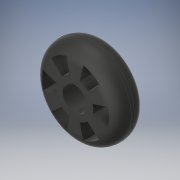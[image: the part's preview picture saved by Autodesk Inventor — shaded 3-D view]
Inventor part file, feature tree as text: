
AUTODESK INVENTOR PART (.ipt)
format: ipt  version: 2017 SP1 (Build 210196100, 196)  size: 229,888 bytes
history: native  units: in
note: dims shown in document units (in); Inventor stores cm internally (conversion verified against a paired STEP export)
features: extrude x1, fillet x1, sketch x1
ambient origin geometry x8: Origin, YZ Plane, XZ Plane, XY Plane, X Axis, Y Axis, Z Axis, Center Point
bodies: Solid1 (feature_tree)
feature tree (3):
  extrude  "Extrusion1"  Depth=0.0886in
  fillet  "Fillet1"  Radius=0.2362in
  sketch  "Sketch1"  dims[d0=0.1575in d1=0.5512in d2=0.2362in d3=0.4331in d4=0.0295in d5=0.0295in d6=2.3622in d8=360.0deg d10=0.1969in d11=0.0in d12=0.0886in]
